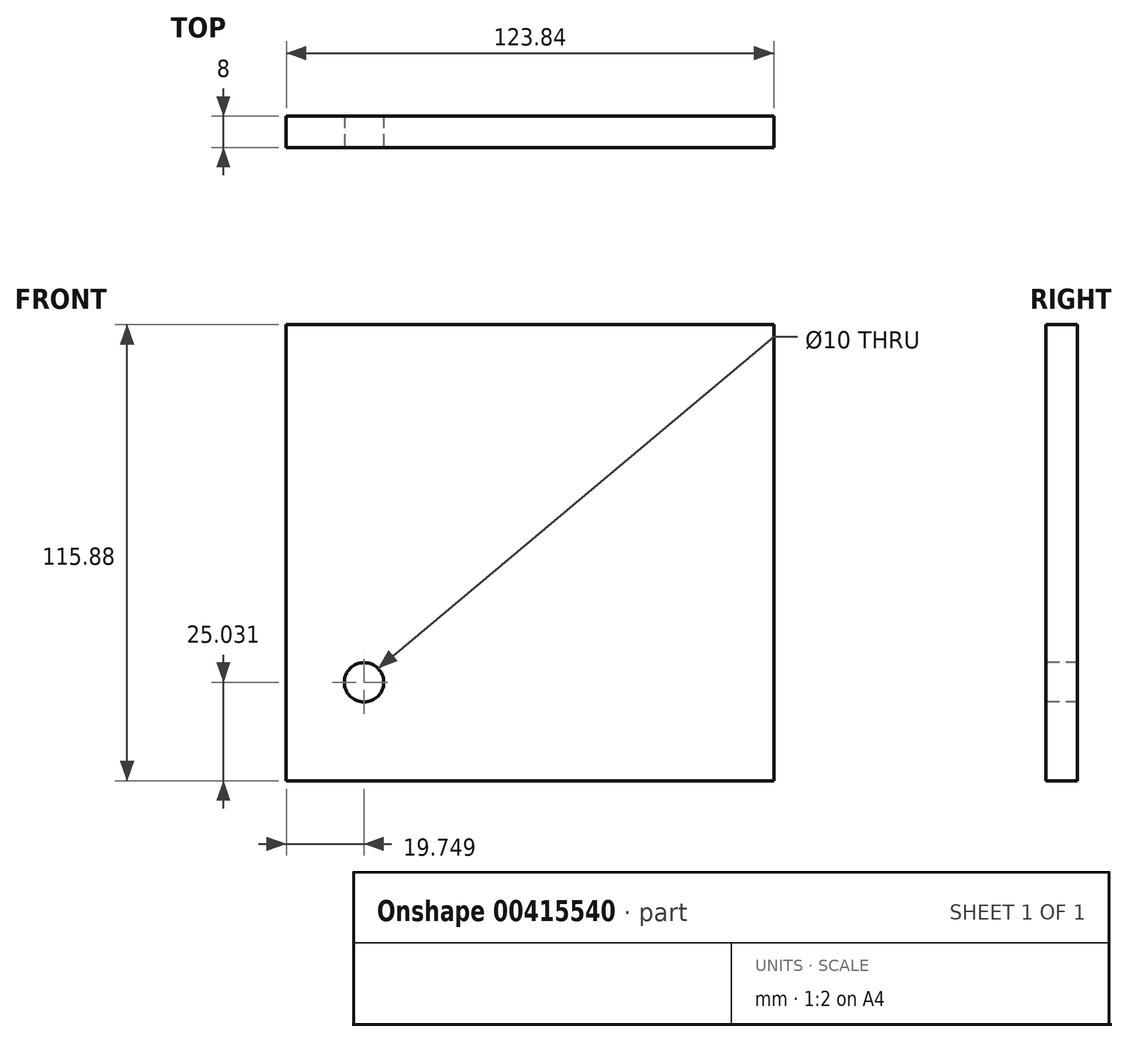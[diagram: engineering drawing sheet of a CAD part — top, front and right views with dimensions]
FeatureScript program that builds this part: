
annotation { "Feature Type Name" : "Feature", "Feature Type Description" : "" }
export const myFeature = defineFeature(function(context is Context, id is Id, definition is map)
    precondition{}
    {
        {
            var Q0;
            Q0=qCreatedBy(makeId("Front.planeOp"),FACE);
            var sketch = newSketch(context, id + "F0", { "sketchPlane" : qUnion([Q0])});
            skLineSegment(sketch, "E0.bottom", {"start": v(-61.8, 56.42) * mm, "end": v(62.04, 56.42) * mm});
            skLineSegment(sketch, "E0.top", {"start": v(-61.8, -59.46) * mm, "end": v(62.04, -59.46) * mm});
            skLineSegment(sketch, "E0.left", {"start": v(-61.8, 56.42) * mm, "end": v(-61.8, -59.46) * mm});
            skLineSegment(sketch, "E0.right", {"start": v(62.04, 56.42) * mm, "end": v(62.04, -59.46) * mm});
            skSolve(sketch);
        }
        {
            var Q0;
            Q0=makeQuery(id+"F0.imprint","IMPRINT",FACE,{"disambiguationData":[TD([[makeQuery(id+"F0.imprint","IMPRINT",EDGE,{"derivedFrom":sQuery(id+"F0.wireOp",EDGE,"E0.bottom")}),-1.0]])]});
            extrude(context, id + "F1", {"entities" : qUnion([Q0]), "depth" : 8 * mm});
        }
        {
            var Q0;
            Q0=makeQuery(id+"F1.opExtrude","SWEPT_FACE",FACE,{"disambiguationData":[OSD([sQuery(id+"F0.wireOp",EDGE,"E0.bottom")])]});
            var sketch = newSketch(context, id + "F2", { "sketchPlane" : qUnion([Q0])});
            skCircle(sketch, "E1", {"center": v(53.26, -3.77) * mm, "radius": 2.06 * mm});
            skSolve(sketch);
        }
        {
            var Q0;
            Q0=makeQuery(id+"F1.opExtrude","CAP_FACE",FACE,{"disambiguationData":[OSD([sQuery(id+"F0.wireOp",EDGE,"E0.bottom"),sQuery(id+"F0.wireOp",EDGE,"E0.top"),sQuery(id+"F0.wireOp",EDGE,"E0.left"),sQuery(id+"F0.wireOp",EDGE,"E0.right")])],"isStart":false});
            var sketch = newSketch(context, id + "F3", { "sketchPlane" : qUnion([Q0])});
            skCircle(sketch, "E2", {"center": v(-42.05, -34.43) * mm, "radius": 8.82 * mm});
            skSolve(sketch);
        }
        {
            var Q0;
            Q0=sQuery(id+"F3.wireOp",VERTEX,"E2.center");
            var Q1;
            Q1=makeQuery(id+"F1.opExtrude","SWEPT_BODY",BODY,{"disambiguationData":[OSD([sQuery(id+"F0.wireOp",EDGE,"E0.bottom"),sQuery(id+"F0.wireOp",EDGE,"E0.top"),sQuery(id+"F0.wireOp",EDGE,"E0.left"),sQuery(id+"F0.wireOp",EDGE,"E0.right")])]});
            hole(context, id + "F4", {"style" : HoleStyle.SIMPLE, "endStyle" : HoleEndStyle.THROUGH, "holeDiameter" : 10 * mm, "isTappedThrough" : true, "tappedDepth" : 12 * mm, "tapClearance" : 3, "locations" : qUnion([Q0]), "scope" : qUnion([Q1])});
        }
    });
